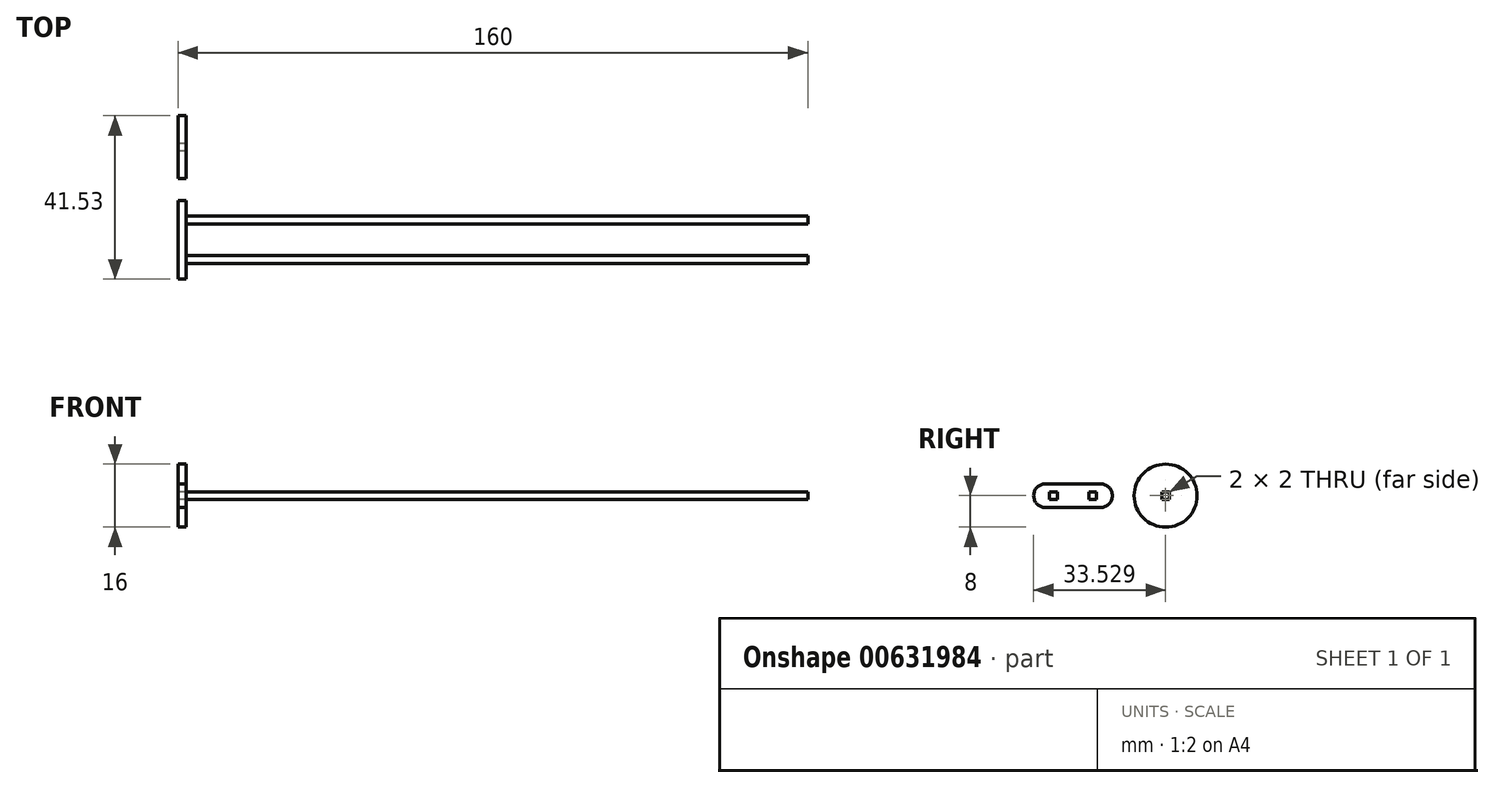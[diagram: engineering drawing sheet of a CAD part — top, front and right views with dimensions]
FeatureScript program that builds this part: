
annotation { "Feature Type Name" : "Feature", "Feature Type Description" : "" }
export const myFeature = defineFeature(function(context is Context, id is Id, definition is map)
    precondition{}
    {
        {
            var Q0;
            Q0=qCreatedBy(makeId("Right.planeOp"),FACE);
            var sketch = newSketch(context, id + "F0", { "sketchPlane" : qUnion([Q0])});
            skLineSegment(sketch, "E0.bottom", {"start": v(7, 3) * mm, "end": v(-7, 3) * mm});
            skLineSegment(sketch, "E0.top", {"start": v(7, -3) * mm, "end": v(-7, -3) * mm});
            skLineSegment(sketch, "E0.left", {"start": v(10, 0) * mm, "end": v(10, 0) * mm});
            skLineSegment(sketch, "E0.right", {"start": v(-10, 0) * mm, "end": v(-10, 0) * mm});
            skPoint(sketch, "E0.middle", {"position": v(0, 0) * mm});
            skPoint(sketch, "E1.visualSharp", {"position": v(-10, 3) * mm});
            skArc(sketch, "E1.filletArc", {"start": v(-7, 3) * mm, "mid": v(-9.12, 2.12) * mm, "end": v(-10, 0) * mm});
            skPoint(sketch, "E2.visualSharp", {"position": v(10, 3) * mm});
            skArc(sketch, "E2.filletArc", {"start": v(10, 0) * mm, "mid": v(9.12, 2.12) * mm, "end": v(7, 3) * mm});
            skPoint(sketch, "E3.visualSharp", {"position": v(10, -3) * mm});
            skArc(sketch, "E3.filletArc", {"start": v(7, -3) * mm, "mid": v(9.12, -2.12) * mm, "end": v(10, 0) * mm});
            skPoint(sketch, "E4.visualSharp", {"position": v(-10, -3) * mm});
            skArc(sketch, "E4.filletArc", {"start": v(-10, 0) * mm, "mid": v(-9.12, -2.12) * mm, "end": v(-7, -3) * mm});
            skLineSegment(sketch, "E5.bottom", {"start": v(-4, -1) * mm, "end": v(-6, -1) * mm});
            skLineSegment(sketch, "E5.top", {"start": v(-4, 1) * mm, "end": v(-6, 1) * mm});
            skLineSegment(sketch, "E5.left", {"start": v(-4, -1) * mm, "end": v(-4, 1) * mm});
            skLineSegment(sketch, "E5.right", {"start": v(-6, -1) * mm, "end": v(-6, 1) * mm});
            skPoint(sketch, "E5.middle", {"position": v(-5, 0) * mm});
            skLineSegment(sketch, "E6.bottom", {"start": v(4, 1) * mm, "end": v(6, 1) * mm});
            skLineSegment(sketch, "E6.top", {"start": v(4, -1) * mm, "end": v(6, -1) * mm});
            skLineSegment(sketch, "E6.left", {"start": v(4, 1) * mm, "end": v(4, -1) * mm});
            skLineSegment(sketch, "E6.right", {"start": v(6, 1) * mm, "end": v(6, -1) * mm});
            skPoint(sketch, "E6.middle", {"position": v(5, 0) * mm});
            skCircle(sketch, "E7", {"center": v(23.53, 0) * mm, "radius": 8 * mm});
            skLineSegment(sketch, "E8.bottom", {"start": v(24.53, -1) * mm, "end": v(22.53, -1) * mm});
            skLineSegment(sketch, "E8.top", {"start": v(24.53, 1) * mm, "end": v(22.53, 1) * mm});
            skLineSegment(sketch, "E8.left", {"start": v(24.53, -1) * mm, "end": v(24.53, 1) * mm});
            skLineSegment(sketch, "E8.right", {"start": v(22.53, -1) * mm, "end": v(22.53, 1) * mm});
            skSolve(sketch);
        }
        {
            var Q0;
            Q0=makeQuery(id+"F0.imprint","IMPRINT",FACE,{"disambiguationData":[TD([[makeQuery(id+"F0.imprint","IMPRINT",EDGE,{"derivedFrom":sQuery(id+"F0.wireOp",EDGE,"E0.bottom")}),1.0]])]});
            var Q1;
            Q1=makeQuery(id+"F0.imprint","IMPRINT",FACE,{"disambiguationData":[TD([[makeQuery(id+"F0.imprint","IMPRINT",EDGE,{"derivedFrom":sQuery(id+"F0.wireOp",EDGE,"E5.bottom")}),-1.0]])]});
            var Q2;
            Q2=makeQuery(id+"F0.imprint","IMPRINT",FACE,{"disambiguationData":[TD([[makeQuery(id+"F0.imprint","IMPRINT",EDGE,{"derivedFrom":sQuery(id+"F0.wireOp",EDGE,"E6.bottom")}),-1.0]])]});
            extrude(context, id + "F1", {"entities" : qUnion([Q0, Q1, Q2]), "depth" : 2 * mm, "offsetDistance" : 25 * mm});
        }
        {
            var Q0;
            Q0=makeQuery(id+"F0.imprint","IMPRINT",FACE,{"disambiguationData":[TD([[makeQuery(id+"F0.imprint","IMPRINT",EDGE,{"derivedFrom":sQuery(id+"F0.wireOp",EDGE,"E5.bottom")}),-1.0]])]});
            var Q1;
            Q1=makeQuery(id+"F0.imprint","IMPRINT",FACE,{"disambiguationData":[TD([[makeQuery(id+"F0.imprint","IMPRINT",EDGE,{"derivedFrom":sQuery(id+"F0.wireOp",EDGE,"E6.bottom")}),-1.0]])]});
            extrude(context, id + "F2", {"entities" : qUnion([Q0, Q1]), "operationType" : NewBodyOperationType.ADD, "depth" : 160 * mm, "offsetDistance" : 25 * mm});
        }
        {
            var Q0;
            Q0=makeQuery(id+"F0.imprint","IMPRINT",FACE,{"disambiguationData":[TD([[makeQuery(id+"F0.imprint","IMPRINT",EDGE,{"derivedFrom":sQuery(id+"F0.wireOp",EDGE,"E7")}),1.0]])]});
            extrude(context, id + "F3", {"entities" : qUnion([Q0]), "depth" : 2 * mm, "offsetDistance" : 25 * mm});
        }
    });
